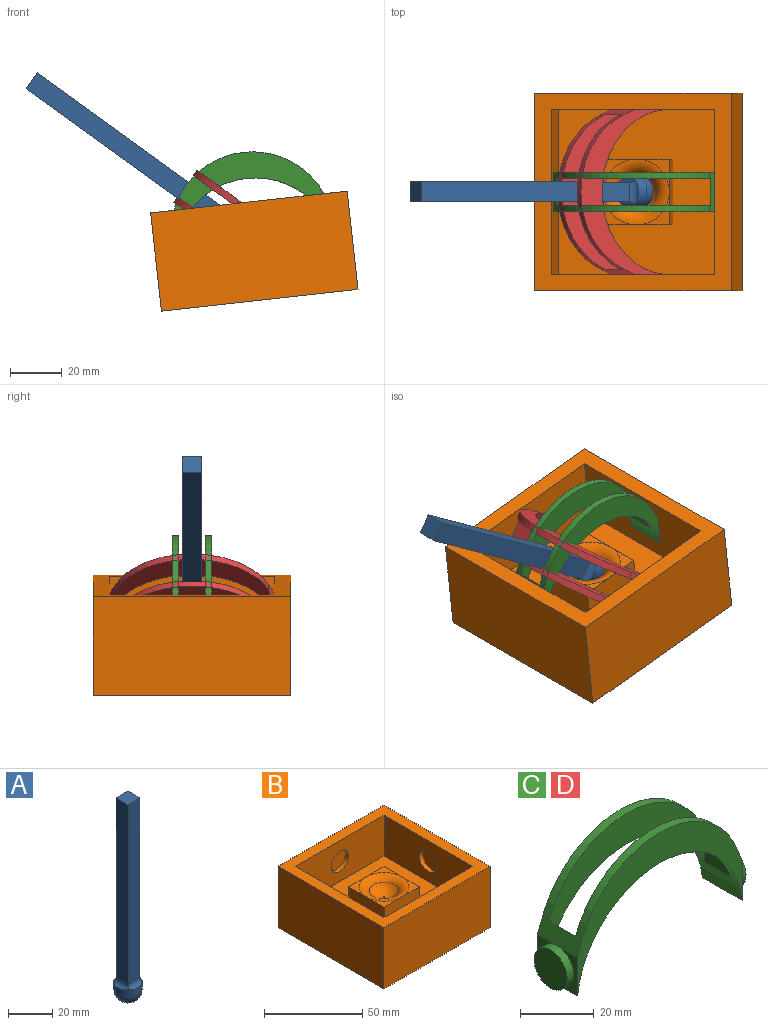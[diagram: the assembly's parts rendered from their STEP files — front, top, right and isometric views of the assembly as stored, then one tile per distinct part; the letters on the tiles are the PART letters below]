
ASSEMBLY  parts=4 mates=4
PART A: 11 faces, bbox 12.7x12.7x111.8 mm
  f0: cylinder r=6.35mm len=12.7mm, axis (0,0,-1), area 158.1mm2, adj f1,f7,f8,f9,f10
  f1: sphere r=6.35mm, area 253.4mm2, adj f0
  f2: plane 99.06x7.62mm, normal (1,0,0), area 754.8mm2, adj f3,f5,f6,f7
  f3: plane 99.06x7.62mm, normal (0,1,0), area 754.8mm2, adj f2,f4,f6,f8
  f4: plane 99.06x7.62mm, normal (-1,0,0), area 754.8mm2, adj f3,f5,f6,f10
  f5: plane 99.06x7.62mm, normal (0,-1,0), area 754.8mm2, adj f2,f4,f6,f9
  f6: plane 7.62x7.62mm, normal (0,0,1), area 58.1mm2, adj f2,f3,f4,f5
  f7: cylinder r=2.54mm len=8.98mm, axis (0,1,0), area 28.7mm2, adj f0,f2,f8,f9
  f8: cylinder r=2.54mm len=8.98mm, axis (-1,0,0), area 28.7mm2, adj f0,f3,f7,f10
  f9: cylinder r=2.54mm len=8.98mm, axis (1,0,0), area 28.7mm2, adj f0,f5,f7,f10
  f10: cylinder r=2.54mm len=8.98mm, axis (0,-1,0), area 28.7mm2, adj f0,f4,f8,f9
PART B: 30 faces, bbox 76.2x76.2x38.1 mm
  f0: plane 12.7x12.7mm, normal (0,0,1), area 34.6mm2, adj f22,f25,f28
  f1: plane 12.7x12.7mm, normal (0,0,1), area 34.6mm2, adj f24,f25,f28
  f2: plane 12.7x12.7mm, normal (0,0,1), area 34.6mm2, adj f23,f24,f28
  f3: plane 76.2x76.2mm, normal (0,0,1), area 1774.2mm2, adj f4,f5,f6,f7,f9,f10,f11,f12
  f4: plane 76.2x38.1mm, normal (0,1,0), area 2903.2mm2, adj f3,f5,f7,f8
  f5: plane 76.2x38.1mm, normal (-1,0,0), area 2903.2mm2, adj f3,f4,f6,f8
  f6: plane 76.2x38.1mm, normal (0,-1,0), area 2903.2mm2, adj f3,f5,f7,f8
  f7: plane 76.2x38.1mm, normal (1,0,0), area 2903.2mm2, adj f3,f4,f6,f8
  f8: plane 76.2x76.2mm, normal (0,0,-1), area 5806.4mm2, adj f4,f5,f6,f7
  f9: plane 63.5x25.4mm, normal (1,0,0), area 1486.2mm2, adj f3,f10,f12,f13,f20
  f10: plane 63.5x25.4mm, normal (0,1,0), area 1486.2mm2, adj f3,f9,f11,f13,f16
  f11: plane 63.5x25.4mm, normal (-1,0,0), area 1486.2mm2, adj f3,f10,f12,f13,f19
  f12: plane 63.5x25.4mm, normal (0,-1,0), area 1486.2mm2, adj f3,f9,f11,f13,f15
  f13: plane 63.5x63.5mm, normal (0,0,1), area 3387.1mm2, adj f9,f10,f11,f12,f22,f23,f24,f25
  f14: plane 12.7x12.7mm, normal (0,-1,0), area 126.7mm2, adj f15
  f15: cylinder r=6.35mm len=12.7mm, axis (0,-1,0), area 101.3mm2, adj f12,f14
  f16: cylinder r=6.35mm len=12.7mm, axis (0,-1,0), area 101.3mm2, adj f10,f17
  f17: plane 12.7x12.7mm, normal (0,1,0), area 126.7mm2, adj f16
  f18: plane 12.7x12.7mm, normal (-1,0,0), area 126.7mm2, adj f19
  f19: cylinder r=6.35mm len=12.7mm, axis (1,0,0), area 101.3mm2, adj f11,f18
  f20: cylinder r=6.35mm len=12.7mm, axis (1,0,0), area 101.3mm2, adj f9,f21
  f21: plane 12.7x12.7mm, normal (1,0,0), area 126.7mm2, adj f20
  f22: plane 25.4x12.7mm, normal (1,0,0), area 322.6mm2, adj f0,f13,f23,f25,f26
  f23: plane 25.4x12.7mm, normal (0,1,0), area 322.6mm2, adj f2,f13,f22,f24,f26
  f24: plane 25.4x12.7mm, normal (-1,0,0), area 322.6mm2, adj f1,f2,f13,f23,f25
  f25: plane 25.4x12.7mm, normal (0,-1,0), area 322.6mm2, adj f0,f1,f13,f22,f24
  f26: plane 12.7x12.7mm, normal (0,0,1), area 34.6mm2, adj f22,f23,f28
  f27: plane 0.03x0.03mm, normal (0,0,1), area 0mm2, adj f29
  f28: torus R=12.7mm, axis (0,0,1), area 368.8mm2, adj f0,f1,f2,f26,f29
  f29: torus R=0.01mm, axis (0,0,-1), area 227.9mm2, adj f27,f28
PART C: 21 faces, bbox 68.6x15.2x38.3 mm
  f0: plane 15.24x0.2mm, normal (0,0,-1), area 3mm2, adj f1,f4,f9,f15,f20
  f1: plane 63.5x38.32mm, normal (0,-1,0), area 647.5mm2, adj f0,f2,f6,f7,f8,f9,f10,f20
  f2: plane 15.24x0.2mm, normal (0,0,-1), area 3mm2, adj f1,f5,f10,f15,f20
  f3: cylinder r=31.75mm len=58.94mm, axis (0,1,0), area 191.9mm2, adj f6,f8,f15,f18
  f4: plane 12.7x7.62mm, normal (1,0,0), area 33.4mm2, adj f0,f6,f13,f15
  f5: plane 12.7x7.62mm, normal (-1,0,0), area 33.4mm2, adj f2,f8,f12,f15
  f6: plane 15.24x5.69mm, normal (0.93,0,0.37), area 83.1mm2, adj f1,f3,f4,f7,f9,f15,f16,f17
  f7: cylinder r=31.75mm len=58.94mm, axis (0,1,0), area 191.9mm2, adj f1,f6,f8,f17
  f8: plane 15.24x5.69mm, normal (-0.93,0,0.37), area 83.1mm2, adj f1,f3,f5,f7,f10,f15,f17,f18
  f9: plane 12.7x7.62mm, normal (1,0,0), area 33.4mm2, adj f0,f1,f6,f13
  f10: plane 12.7x7.62mm, normal (-1,0,0), area 33.4mm2, adj f1,f2,f8,f12
  f11: plane 12.7x12.7mm, normal (-1,0,0), area 126.7mm2, adj f12
  f12: cylinder r=6.35mm len=12.7mm, axis (-1,0,0), area 101.3mm2, adj f5,f10,f11
  f13: cylinder r=6.35mm len=12.7mm, axis (-1,0,0), area 101.3mm2, adj f4,f9,f14
  f14: plane 12.7x12.7mm, normal (1,0,0), area 126.7mm2, adj f13
  f15: plane 63.5x38.32mm, normal (0,1,0), area 647.5mm2, adj f0,f2,f3,f4,f5,f6,f8,f20
  f16: plane 10.18x10.16mm, normal (-1,0,0), area 103.4mm2, adj f6,f17,f18,f20
  f17: plane 59.69x31.05mm, normal (0,1,0), area 604.6mm2, adj f6,f7,f8,f16,f19,f20
  f18: plane 59.69x31.05mm, normal (0,-1,0), area 604.6mm2, adj f3,f6,f8,f16,f19,f20
  f19: plane 10.18x10.16mm, normal (1,0,0), area 103.4mm2, adj f8,f17,f18,f20
  f20: cylinder r=31.75mm len=63.1mm, axis (0,-1,0), area 622.8mm2, adj f0,f1,f2,f15,f16,f17,f18,f19
PART D: same geometry as C
PLACE A rot(axis=(0,-1,0),54.1deg) t=(-20.81,-5.31,15.86)mm
PLACE B rot(axis=(0,-1,0),6.3deg) t=(-23.44,-5.31,-3.13)mm fixed
PLACE C rot(axis=(0.06,0,-1),180deg) t=(-25.54,-5.31,15.8)mm
PLACE D rot(axis=(-0.41,-0.41,0.81),101.9deg) t=(-21.09,-5.31,18.39)mm
MATE revolute C.f12 <-> B.f19  axis (-0.99,0,-0.11) through (-60.32,-5.31,18.33)mm
MATE revolute D.f12 <-> B.f15  axis (0,1,0) through (-26.23,28.98,22.11)mm
MATE parallel D.f17 <-> A.f4  axis (-0.59,0,-0.81) through (-40.44,-5.31,38.68)mm
MATE parallel A.f3 <-> C.f18  axis (0,1,0) through (-71.2,-1.5,52.37)mm
